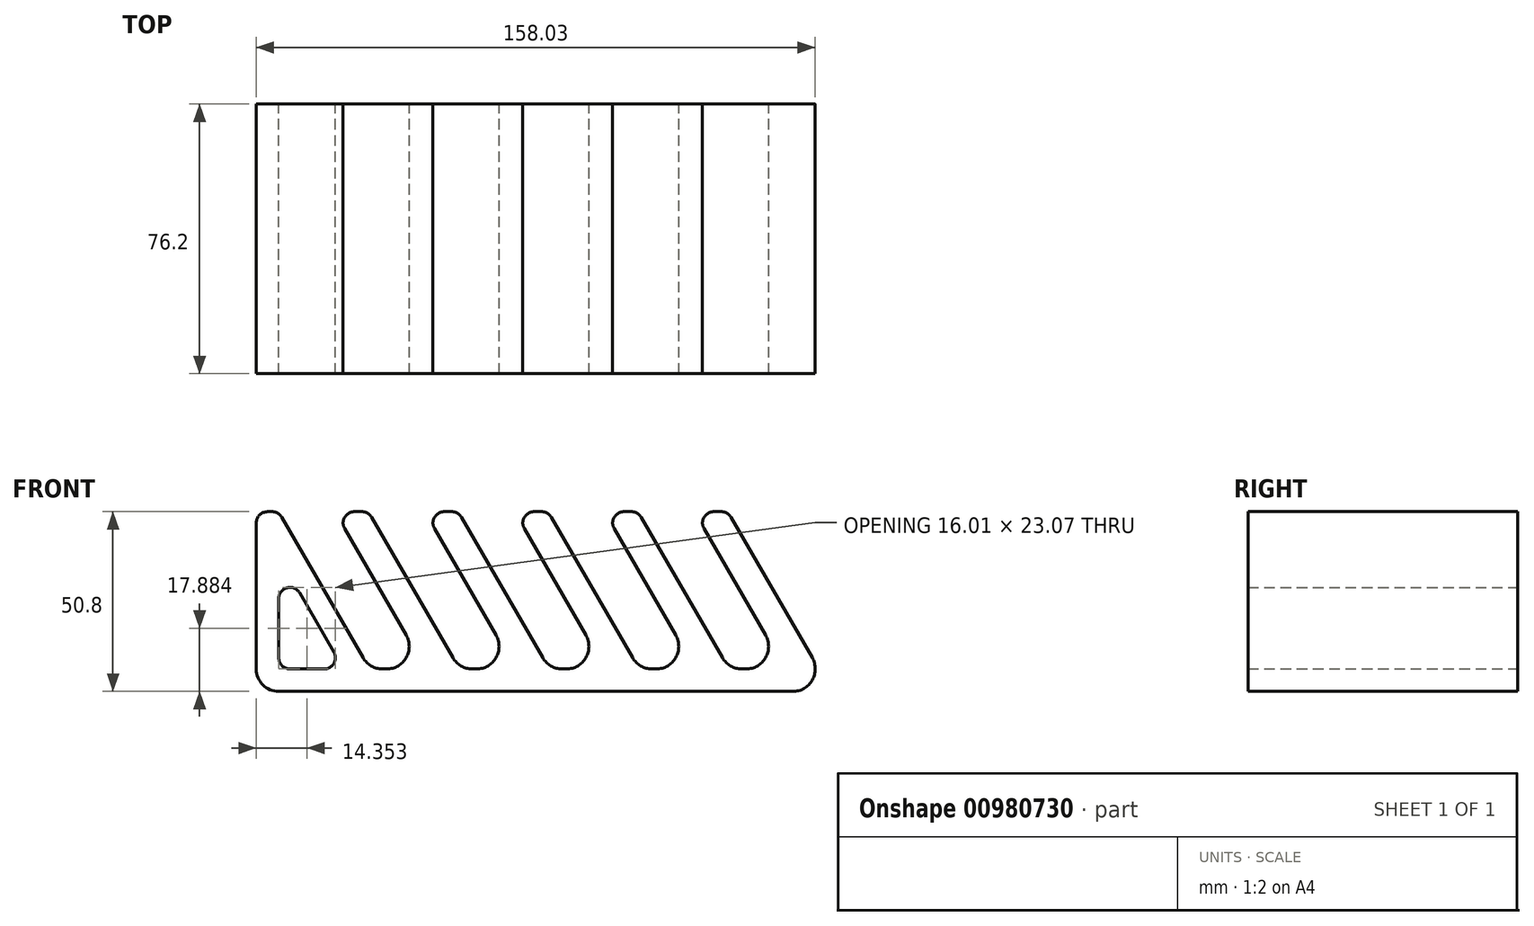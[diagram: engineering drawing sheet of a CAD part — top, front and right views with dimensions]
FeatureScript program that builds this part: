
annotation { "Feature Type Name" : "Feature", "Feature Type Description" : "" }
export const myFeature = defineFeature(function(context is Context, id is Id, definition is map)
    precondition{}
    {
        {
            var Q0;
            Q0=qCreatedBy(makeId("Front.planeOp"),FACE);
            var sketch = newSketch(context, id + "F0", { "sketchPlane" : qUnion([Q0])});
            skLineSegment(sketch, "E0", {"start": v(0, 6.35) * mm, "end": v(0, 47.62) * mm});
            skLineSegment(sketch, "E1", {"start": v(3.17, 50.8) * mm, "end": v(4.52, 50.8) * mm});
            skLineSegment(sketch, "E2", {"start": v(7.27, 49.21) * mm, "end": v(30.18, 9.52) * mm});
            skLineSegment(sketch, "E3", {"start": v(35.68, 6.35) * mm, "end": v(36.89, 6.35) * mm});
            skLineSegment(sketch, "E4", {"start": v(42.39, 15.88) * mm, "end": v(24.97, 46.04) * mm});
            skLineSegment(sketch, "E5", {"start": v(27.72, 50.8) * mm, "end": v(29.92, 50.8) * mm});
            skLineSegment(sketch, "E6", {"start": v(32.67, 49.21) * mm, "end": v(55.58, 9.52) * mm});
            skLineSegment(sketch, "E7", {"start": v(61.08, 6.35) * mm, "end": v(62.29, 6.35) * mm});
            skLineSegment(sketch, "E8", {"start": v(67.79, 15.88) * mm, "end": v(50.37, 46.04) * mm});
            skLineSegment(sketch, "E9", {"start": v(53.12, 50.8) * mm, "end": v(55.32, 50.8) * mm});
            skLineSegment(sketch, "E10", {"start": v(58.07, 49.21) * mm, "end": v(80.98, 9.53) * mm});
            skLineSegment(sketch, "E11", {"start": v(86.48, 6.35) * mm, "end": v(87.69, 6.35) * mm});
            skLineSegment(sketch, "E12", {"start": v(93.19, 15.88) * mm, "end": v(75.77, 46.04) * mm});
            skLineSegment(sketch, "E13", {"start": v(78.52, 50.8) * mm, "end": v(80.72, 50.8) * mm});
            skLineSegment(sketch, "E14", {"start": v(83.47, 49.21) * mm, "end": v(106.38, 9.52) * mm});
            skLineSegment(sketch, "E15", {"start": v(111.88, 6.35) * mm, "end": v(113.09, 6.35) * mm});
            skLineSegment(sketch, "E16", {"start": v(118.59, 15.88) * mm, "end": v(101.17, 46.04) * mm});
            skLineSegment(sketch, "E17", {"start": v(103.92, 50.8) * mm, "end": v(106.12, 50.8) * mm});
            skLineSegment(sketch, "E18", {"start": v(108.87, 49.21) * mm, "end": v(131.78, 9.53) * mm});
            skLineSegment(sketch, "E19", {"start": v(137.28, 6.35) * mm, "end": v(138.49, 6.35) * mm});
            skLineSegment(sketch, "E20", {"start": v(143.99, 15.88) * mm, "end": v(126.57, 46.04) * mm});
            skLineSegment(sketch, "E21", {"start": v(129.32, 50.8) * mm, "end": v(131.52, 50.8) * mm});
            skLineSegment(sketch, "E22", {"start": v(134.27, 49.21) * mm, "end": v(157.18, 9.53) * mm});
            skLineSegment(sketch, "E23", {"start": v(151.68, 0) * mm, "end": v(6.35, 0) * mm});
            skPoint(sketch, "E24.visualSharp", {"position": v(32.01, 6.35) * mm});
            skArc(sketch, "E24.filletArc", {"start": v(30.18, 9.53) * mm, "mid": v(32.5, 7.2) * mm, "end": v(35.68, 6.35) * mm});
            skPoint(sketch, "E25.visualSharp", {"position": v(47.89, 6.35) * mm});
            skArc(sketch, "E25.filletArc", {"start": v(36.89, 6.35) * mm, "mid": v(42.39, 9.53) * mm, "end": v(42.39, 15.88) * mm});
            skPoint(sketch, "E26.visualSharp", {"position": v(57.41, 6.35) * mm});
            skArc(sketch, "E26.filletArc", {"start": v(55.58, 9.52) * mm, "mid": v(57.9, 7.2) * mm, "end": v(61.08, 6.35) * mm});
            skPoint(sketch, "E27.visualSharp", {"position": v(73.29, 6.35) * mm});
            skArc(sketch, "E27.filletArc", {"start": v(62.29, 6.35) * mm, "mid": v(67.79, 9.53) * mm, "end": v(67.79, 15.88) * mm});
            skPoint(sketch, "E28.visualSharp", {"position": v(82.81, 6.35) * mm});
            skArc(sketch, "E28.filletArc", {"start": v(80.98, 9.53) * mm, "mid": v(83.3, 7.2) * mm, "end": v(86.48, 6.35) * mm});
            skPoint(sketch, "E29.visualSharp", {"position": v(98.69, 6.35) * mm});
            skArc(sketch, "E29.filletArc", {"start": v(87.69, 6.35) * mm, "mid": v(93.19, 9.53) * mm, "end": v(93.19, 15.88) * mm});
            skPoint(sketch, "E30.visualSharp", {"position": v(108.21, 6.35) * mm});
            skArc(sketch, "E30.filletArc", {"start": v(106.38, 9.53) * mm, "mid": v(108.7, 7.2) * mm, "end": v(111.88, 6.35) * mm});
            skPoint(sketch, "E31.visualSharp", {"position": v(124.09, 6.35) * mm});
            skArc(sketch, "E31.filletArc", {"start": v(113.09, 6.35) * mm, "mid": v(118.59, 9.53) * mm, "end": v(118.59, 15.88) * mm});
            skPoint(sketch, "E32.visualSharp", {"position": v(133.61, 6.35) * mm});
            skArc(sketch, "E32.filletArc", {"start": v(131.78, 9.53) * mm, "mid": v(134.1, 7.2) * mm, "end": v(137.28, 6.35) * mm});
            skPoint(sketch, "E33.visualSharp", {"position": v(149.49, 6.35) * mm});
            skArc(sketch, "E33.filletArc", {"start": v(138.49, 6.35) * mm, "mid": v(143.99, 9.53) * mm, "end": v(143.99, 15.88) * mm});
            skPoint(sketch, "E34.visualSharp", {"position": v(162.68, 0) * mm});
            skArc(sketch, "E34.filletArc", {"start": v(151.68, 0) * mm, "mid": v(157.18, 3.18) * mm, "end": v(157.18, 9.53) * mm});
            skPoint(sketch, "E35.visualSharp", {"position": v(0, 0) * mm});
            skArc(sketch, "E35.filletArc", {"start": v(0, 6.35) * mm, "mid": v(1.86, 1.86) * mm, "end": v(6.35, 0) * mm});
            skPoint(sketch, "E36.visualSharp", {"position": v(6.35, 50.8) * mm});
            skArc(sketch, "E36.filletArc", {"start": v(7.27, 49.21) * mm, "mid": v(6.1, 50.37) * mm, "end": v(4.52, 50.8) * mm});
            skPoint(sketch, "E37.visualSharp", {"position": v(22.23, 50.8) * mm});
            skArc(sketch, "E37.filletArc", {"start": v(27.72, 50.8) * mm, "mid": v(24.97, 49.21) * mm, "end": v(24.97, 46.04) * mm});
            skPoint(sketch, "E38.visualSharp", {"position": v(31.75, 50.8) * mm});
            skArc(sketch, "E38.filletArc", {"start": v(32.67, 49.21) * mm, "mid": v(31.5, 50.37) * mm, "end": v(29.92, 50.8) * mm});
            skPoint(sketch, "E39.visualSharp", {"position": v(47.62, 50.8) * mm});
            skArc(sketch, "E39.filletArc", {"start": v(53.12, 50.8) * mm, "mid": v(50.37, 49.21) * mm, "end": v(50.37, 46.04) * mm});
            skPoint(sketch, "E40.visualSharp", {"position": v(57.15, 50.8) * mm});
            skArc(sketch, "E40.filletArc", {"start": v(58.07, 49.21) * mm, "mid": v(56.9, 50.37) * mm, "end": v(55.32, 50.8) * mm});
            skPoint(sketch, "E41.visualSharp", {"position": v(73.02, 50.8) * mm});
            skArc(sketch, "E41.filletArc", {"start": v(78.52, 50.8) * mm, "mid": v(75.77, 49.21) * mm, "end": v(75.77, 46.04) * mm});
            skPoint(sketch, "E42.visualSharp", {"position": v(82.55, 50.8) * mm});
            skArc(sketch, "E42.filletArc", {"start": v(83.47, 49.21) * mm, "mid": v(82.3, 50.37) * mm, "end": v(80.72, 50.8) * mm});
            skPoint(sketch, "E43.visualSharp", {"position": v(98.42, 50.8) * mm});
            skArc(sketch, "E43.filletArc", {"start": v(103.92, 50.8) * mm, "mid": v(101.17, 49.21) * mm, "end": v(101.17, 46.04) * mm});
            skPoint(sketch, "E44.visualSharp", {"position": v(107.95, 50.8) * mm});
            skArc(sketch, "E44.filletArc", {"start": v(108.87, 49.21) * mm, "mid": v(107.7, 50.37) * mm, "end": v(106.12, 50.8) * mm});
            skPoint(sketch, "E45.visualSharp", {"position": v(123.82, 50.8) * mm});
            skArc(sketch, "E45.filletArc", {"start": v(129.32, 50.8) * mm, "mid": v(126.57, 49.21) * mm, "end": v(126.57, 46.04) * mm});
            skPoint(sketch, "E46.visualSharp", {"position": v(133.35, 50.8) * mm});
            skArc(sketch, "E46.filletArc", {"start": v(134.27, 49.21) * mm, "mid": v(133.1, 50.37) * mm, "end": v(131.52, 50.8) * mm});
            skPoint(sketch, "E47.visualSharp", {"position": v(0, 50.8) * mm});
            skArc(sketch, "E47.filletArc", {"start": v(3.17, 50.8) * mm, "mid": v(0.93, 49.87) * mm, "end": v(0, 47.62) * mm});
            skLineSegment(sketch, "E48.0", {"start": v(12.27, 27.84) * mm, "end": v(21.93, 11.11) * mm});
            skLineSegment(sketch, "E49.0", {"start": v(6.35, 9.52) * mm, "end": v(6.35, 26.25) * mm});
            skLineSegment(sketch, "E50", {"start": v(9.53, 6.35) * mm, "end": v(19.18, 6.35) * mm});
            skPoint(sketch, "E51.visualSharp", {"position": v(6.35, 38.1) * mm});
            skArc(sketch, "E51.filletArc", {"start": v(12.27, 27.84) * mm, "mid": v(8.7, 29.32) * mm, "end": v(6.35, 26.25) * mm});
            skPoint(sketch, "E52.visualSharp", {"position": v(24.68, 6.35) * mm});
            skArc(sketch, "E52.filletArc", {"start": v(19.18, 6.35) * mm, "mid": v(21.93, 7.94) * mm, "end": v(21.93, 11.11) * mm});
            skArc(sketch, "E53", {"start": v(6.35, 9.52) * mm, "mid": v(7.28, 7.28) * mm, "end": v(9.53, 6.35) * mm});
            skSolve(sketch);
        }
        {
            var Q0;
            Q0 = qSketchRegion(id + "F0", true);
            extrude(context, id + "F1", {"entities" : qUnion([Q0]), "depth" : 76.2 * mm, "offsetDistance" : 25.4 * mm});
        }
    });
